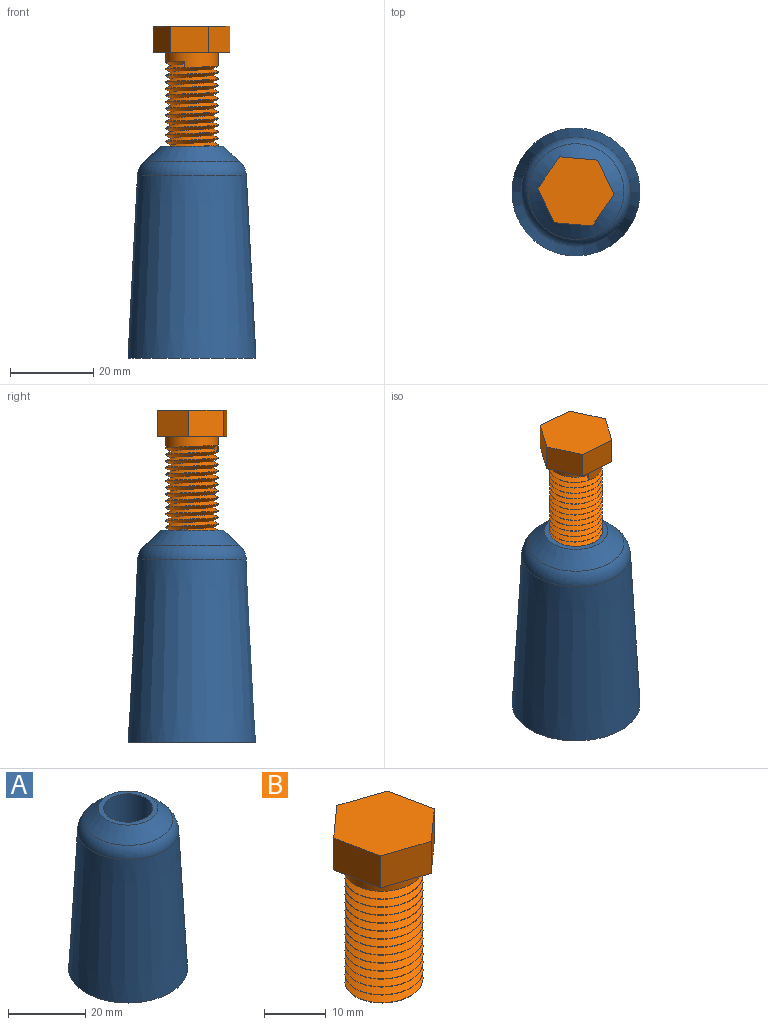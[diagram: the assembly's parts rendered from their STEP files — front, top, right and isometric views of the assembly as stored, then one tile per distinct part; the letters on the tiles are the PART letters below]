
ASSEMBLY  parts=2 mates=1
PART A: 7 faces, bbox 30.7x30.7x50.8 mm
  f0: plane 12.7x12.7mm, normal (0,0,1), area 126.7mm2, adj f1
  f1: cylinder r=6.35mm len=25.4mm, axis (0,0,-1), area 1013.4mm2, adj f0,f3
  f2: cone r=12.7mm half-angle=3deg, axis (0,0,-1), area 3909.3mm2, adj f4,f6
  f3: plane 15.24x15.24mm, normal (0,0,1), area 55.7mm2, adj f1,f5
  f4: plane 30.72x30.72mm, normal (0,0,-1), area 741.4mm2, adj f2
  f5: cone r=7.62mm half-angle=46.5deg, axis (0,0,-1), area 320.9mm2, adj f3,f6
  f6: torus R=8mm, axis (0,0,1), area 303mm2, adj f2,f5
PART B: 27 faces, bbox 18.5x19x33.8 mm
  f0: cylinder r=6.35mm len=12.7mm, axis (0,0,1), area 1.8mm2, adj f1,f15,f24,f25
  f1: cylinder r=6.35mm len=12.7mm, axis (0,0,1), area 2.5mm2, adj f0,f2,f24,f25
  f2: cylinder r=6.35mm len=12.7mm, axis (0,0,1), area 2.5mm2, adj f1,f3,f24,f25
  f3: cylinder r=6.35mm len=12.7mm, axis (0,0,1), area 2.5mm2, adj f2,f4,f24,f25
  f4: cylinder r=6.35mm len=12.7mm, axis (0,0,1), area 2.5mm2, adj f3,f5,f24,f25
  f5: cylinder r=6.35mm len=12.7mm, axis (0,0,1), area 2.6mm2, adj f4,f6,f24,f25
  f6: cylinder r=6.35mm len=12.7mm, axis (0,0,1), area 2.5mm2, adj f5,f7,f24,f25
  f7: cylinder r=6.35mm len=12.7mm, axis (0,0,1), area 2.5mm2, adj f6,f8,f24,f25
  f8: cylinder r=6.35mm len=12.7mm, axis (0,0,1), area 2.5mm2, adj f7,f9,f24,f25
  f9: cylinder r=6.35mm len=12.7mm, axis (0,0,1), area 2.6mm2, adj f8,f10,f24,f25
  f10: cylinder r=6.35mm len=12.7mm, axis (0,0,1), area 2.5mm2, adj f9,f11,f24,f25
  f11: cylinder r=6.35mm len=12.7mm, axis (0,0,1), area 2.5mm2, adj f10,f12,f24,f25
  f12: cylinder r=6.35mm len=12.7mm, axis (0,0,1), area 2.5mm2, adj f11,f13,f24,f25
  f13: cylinder r=6.35mm len=12.7mm, axis (0,0,1), area 2.5mm2, adj f12,f14,f24,f25
  f14: cylinder r=6.35mm len=12.7mm, axis (0,0,1), area 114.3mm2, adj f13,f23,f24,f26
  f15: plane 12.57x12.56mm, normal (0,0,-1), area 103.1mm2, adj f0,f24,f25
  f16: plane 6.85x6.35mm, normal (0.66,-0.75,0), area 58.2mm2, adj f17,f21,f22,f23
  f17: plane 8.98x6.35mm, normal (0.98,0.2,0), area 58.2mm2, adj f16,f18,f22,f23
  f18: plane 8.7x6.35mm, normal (0.32,0.95,0), area 58.2mm2, adj f17,f19,f22,f23
  f19: plane 6.85x6.35mm, normal (-0.66,0.75,0), area 58.2mm2, adj f18,f20,f22,f23
  f20: plane 8.98x6.35mm, normal (-0.98,-0.2,0), area 58.2mm2, adj f19,f21,f22,f23
  f21: plane 8.7x6.35mm, normal (-0.32,-0.95,0), area 58.2mm2, adj f16,f20,f22,f23
  f22: plane 17.96x17.39mm, normal (0,0,1), area 218.3mm2, adj f16,f17,f18,f19,f20,f21
  f23: plane 17.96x17.39mm, normal (0,0,-1), area 91.6mm2, adj f14,f16,f17,f18,f19,f20,f21
  f24: bspline ~24.31x14.66mm, area 789.6mm2, adj f0,f1,f2,f3,f4,f5,f6,f7
  f25: bspline ~23.52x14.66mm, area 761.6mm2, adj f0,f1,f2,f3,f4,f5,f6,f7
  f26: plane 1.52x1.32mm, normal (0,-1,0), area 1mm2, adj f14,f24,f25
PLACE A at identity fixed
PLACE B rot(axis=(0,0,-1),106.6deg) t=(0,0,73.32)mm
MATE cylindrical A.f1 <-> B.f0  axis (0,0,-1) through (0,0,50.8)mm
